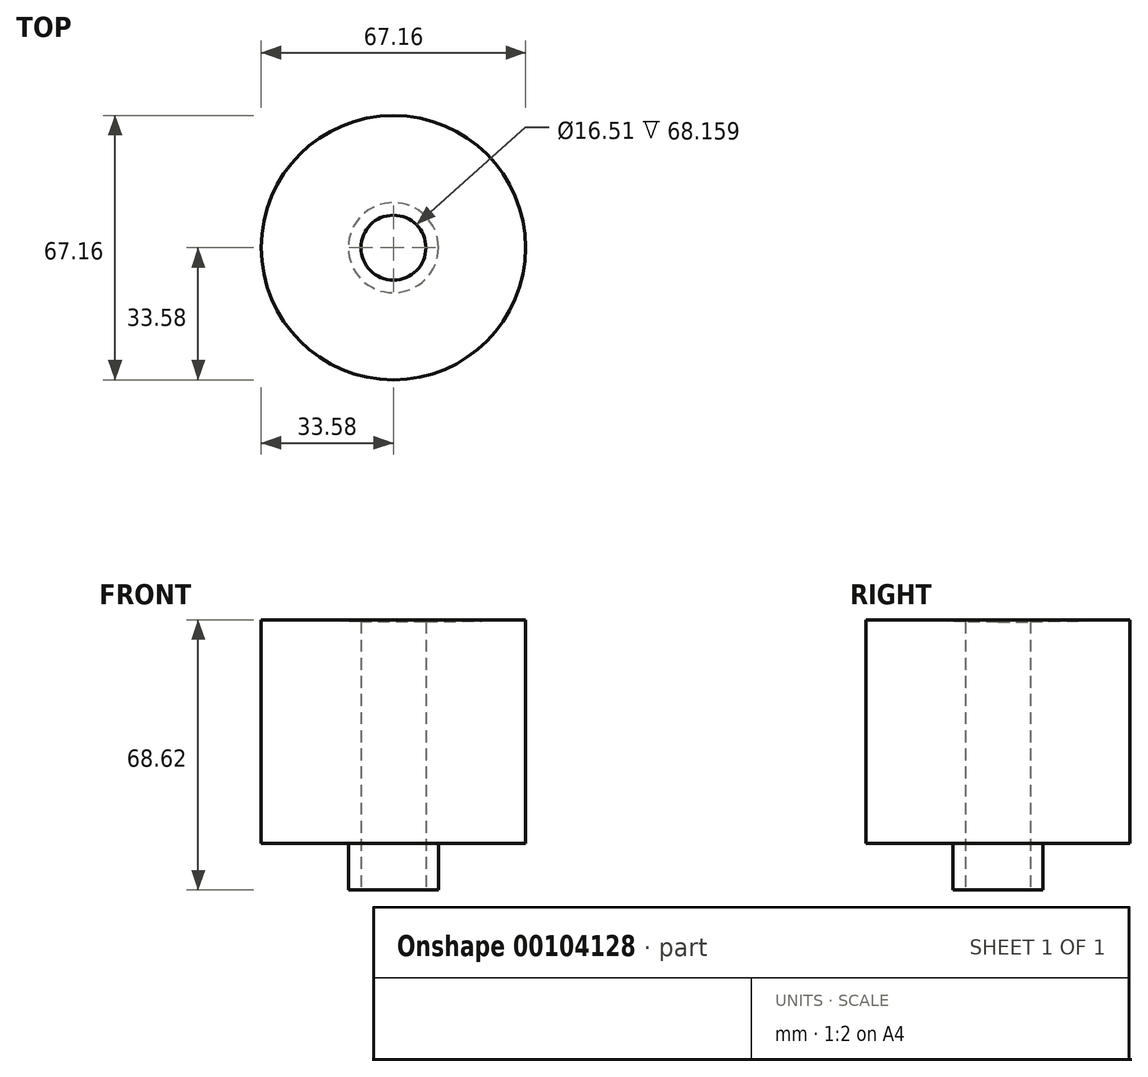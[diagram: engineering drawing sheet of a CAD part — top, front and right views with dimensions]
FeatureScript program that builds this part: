
annotation { "Feature Type Name" : "Feature", "Feature Type Description" : "" }
export const myFeature = defineFeature(function(context is Context, id is Id, definition is map)
    precondition{}
    {
        {
            var Q0;
            Q0=qCreatedBy(makeId("Front.planeOp"),FACE);
            var sketch = newSketch(context, id + "F0", { "sketchPlane" : qUnion([Q0])});
            skLineSegment(sketch, "E0", {"start": v(0, 56.17) * mm, "end": v(0, 0) * mm});
            skLineSegment(sketch, "E1", {"start": v(0, 0) * mm, "end": v(33.58, 0) * mm});
            skLineSegment(sketch, "E2", {"start": v(33.58, 0) * mm, "end": v(33.58, 56.78) * mm});
            skLineSegment(sketch, "E3", {"start": v(33.58, 56.78) * mm, "end": v(0, 56.17) * mm});
            skSolve(sketch);
        }
        {
            var Q0;
            Q0=makeQuery(id+"F0.imprint","IMPRINT",FACE,{"disambiguationData":[TD([[makeQuery(id+"F0.imprint","IMPRINT",EDGE,{"derivedFrom":sQuery(id+"F0.wireOp",EDGE,"E0")}),1.0]])]});
            var Q1;
            Q1=sQuery(id+"F0.wireOp",EDGE,"E0");
            revolve(context, id + "F1", {"entities" : qUnion([Q0]), "axis" : qUnion([Q1]), "revolveType" : RevolveType.FULL});
        }
        {
            var Q0;
            Q0=makeQuery(id+"F1.opRevolve","SWEPT_FACE",FACE,{"disambiguationData":[OSD([sQuery(id+"F0.wireOp",EDGE,"E1")])]});
            var sketch = newSketch(context, id + "F2", { "sketchPlane" : qUnion([Q0])});
            skCircle(sketch, "E4", {"center": v(0, 0) * mm, "radius": 11.44 * mm});
            skSolve(sketch);
        }
        {
            var Q0;
            Q0=makeQuery(id+"F2.imprint","IMPRINT",FACE,{"disambiguationData":[TD([[makeQuery(id+"F2.imprint","IMPRINT",EDGE,{"derivedFrom":sQuery(id+"F2.wireOp",EDGE,"E4")}),1.0]])]});
            extrude(context, id + "F3", {"entities" : qUnion([Q0]), "operationType" : NewBodyOperationType.ADD, "depth" : 11.84 * mm});
        }
        {
            var Q0;
            Q0=makeQuery(id+"F3.opExtrude","CAP_FACE",FACE,{"disambiguationData":[OSD([sQuery(id+"F2.wireOp",EDGE,"E4")])],"isStart":false});
            var sketch = newSketch(context, id + "F4", { "sketchPlane" : qUnion([Q0])});
            skCircle(sketch, "E5", {"center": v(0, 0) * mm, "radius": 8.25 * mm});
            skSolve(sketch);
        }
        {
            var Q0;
            Q0=makeQuery(id+"F4.imprint","IMPRINT",FACE,{"disambiguationData":[TD([[makeQuery(id+"F4.imprint","IMPRINT",EDGE,{"derivedFrom":sQuery(id+"F4.wireOp",EDGE,"E5")}),1.0]])]});
            extrude(context, id + "F5", {"entities" : qUnion([Q0]), "operationType" : NewBodyOperationType.REMOVE, "oppositeDirection" : true, "depth" : 104.95 * mm});
        }
    });
